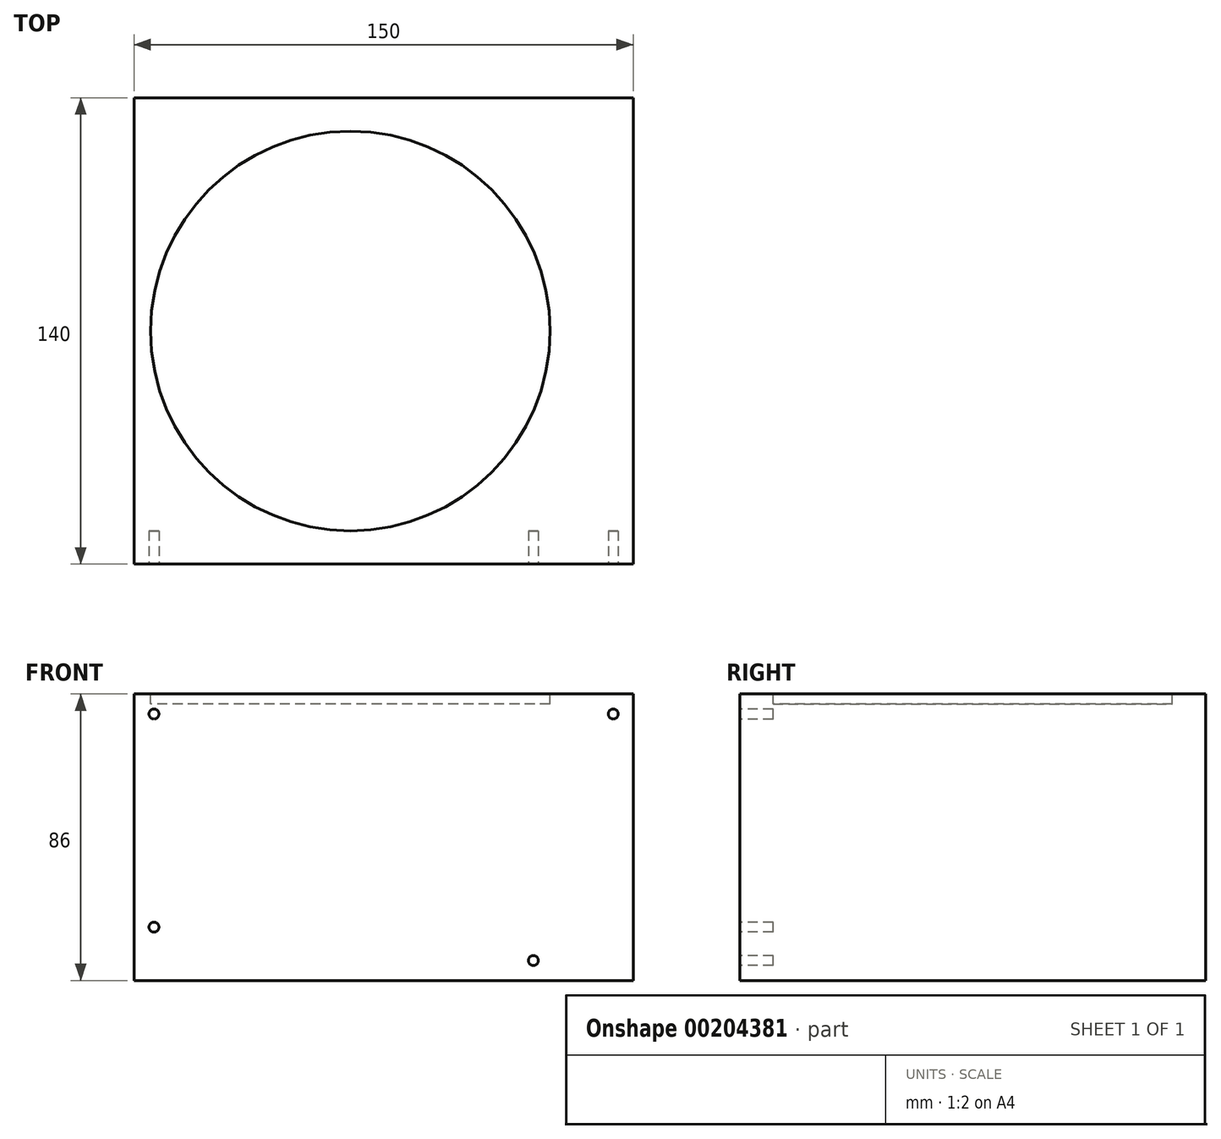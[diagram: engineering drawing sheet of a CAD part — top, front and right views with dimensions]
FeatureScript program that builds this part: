
annotation { "Feature Type Name" : "Feature", "Feature Type Description" : "" }
export const myFeature = defineFeature(function(context is Context, id is Id, definition is map)
    precondition{}
    {
        {
            var Q0;
            Q0=qCreatedBy(makeId("Top.planeOp"),FACE);
            var sketch = newSketch(context, id + "F0", { "sketchPlane" : qUnion([Q0])});
            skLineSegment(sketch, "E0.bottom", {"start": v(0, 0) * mm, "end": v(150, 0) * mm});
            skLineSegment(sketch, "E0.top", {"start": v(0, 140) * mm, "end": v(150, 140) * mm});
            skLineSegment(sketch, "E0.left", {"start": v(0, 0) * mm, "end": v(0, 140) * mm});
            skLineSegment(sketch, "E0.right", {"start": v(150, 0) * mm, "end": v(150, 140) * mm});
            skSolve(sketch);
        }
        {
            var Q0;
            Q0 = qSketchRegion(id + "F0", true);
            extrude(context, id + "F1", {"entities" : qUnion([Q0]), "depth" : 86 * mm});
        }
        {
            var Q0;
            Q0=makeQuery(id+"F1.opExtrude","SWEPT_FACE",FACE,{"disambiguationData":[OSD([sQuery(id+"F0.wireOp",EDGE,"E0.bottom")])]});
            var sketch = newSketch(context, id + "F2", { "sketchPlane" : qUnion([Q0])});
            skCircle(sketch, "E1", {"center": v(6, 80) * mm, "radius": 1.5 * mm});
            skCircle(sketch, "E2", {"center": v(6, 16) * mm, "radius": 1.5 * mm});
            skCircle(sketch, "E3", {"center": v(144, 80) * mm, "radius": 1.5 * mm});
            skCircle(sketch, "E4", {"center": v(120, 6) * mm, "radius": 1.5 * mm});
            skSolve(sketch);
        }
        {
            var Q0;
            Q0 = qSketchRegion(id + "F2", true);
            extrude(context, id + "F3", {"entities" : qUnion([Q0]), "operationType" : NewBodyOperationType.REMOVE, "oppositeDirection" : true, "depth" : 10 * mm});
        }
        {
            var Q0;
            Q0=makeQuery(id+"F1.opExtrude","CAP_FACE",FACE,{"disambiguationData":[OSD([sQuery(id+"F0.wireOp",EDGE,"E0.bottom"),sQuery(id+"F0.wireOp",EDGE,"E0.top"),sQuery(id+"F0.wireOp",EDGE,"E0.left"),sQuery(id+"F0.wireOp",EDGE,"E0.right")])],"isStart":false});
            var sketch = newSketch(context, id + "F4", { "sketchPlane" : qUnion([Q0])});
            skCircle(sketch, "E5", {"center": v(65, 70) * mm, "radius": 60 * mm});
            skSolve(sketch);
        }
        {
            var Q0;
            Q0 = qSketchRegion(id + "F4", true);
            extrude(context, id + "F5", {"entities" : qUnion([Q0]), "operationType" : NewBodyOperationType.REMOVE, "oppositeDirection" : true, "depth" : 3 * mm});
        }
    });
